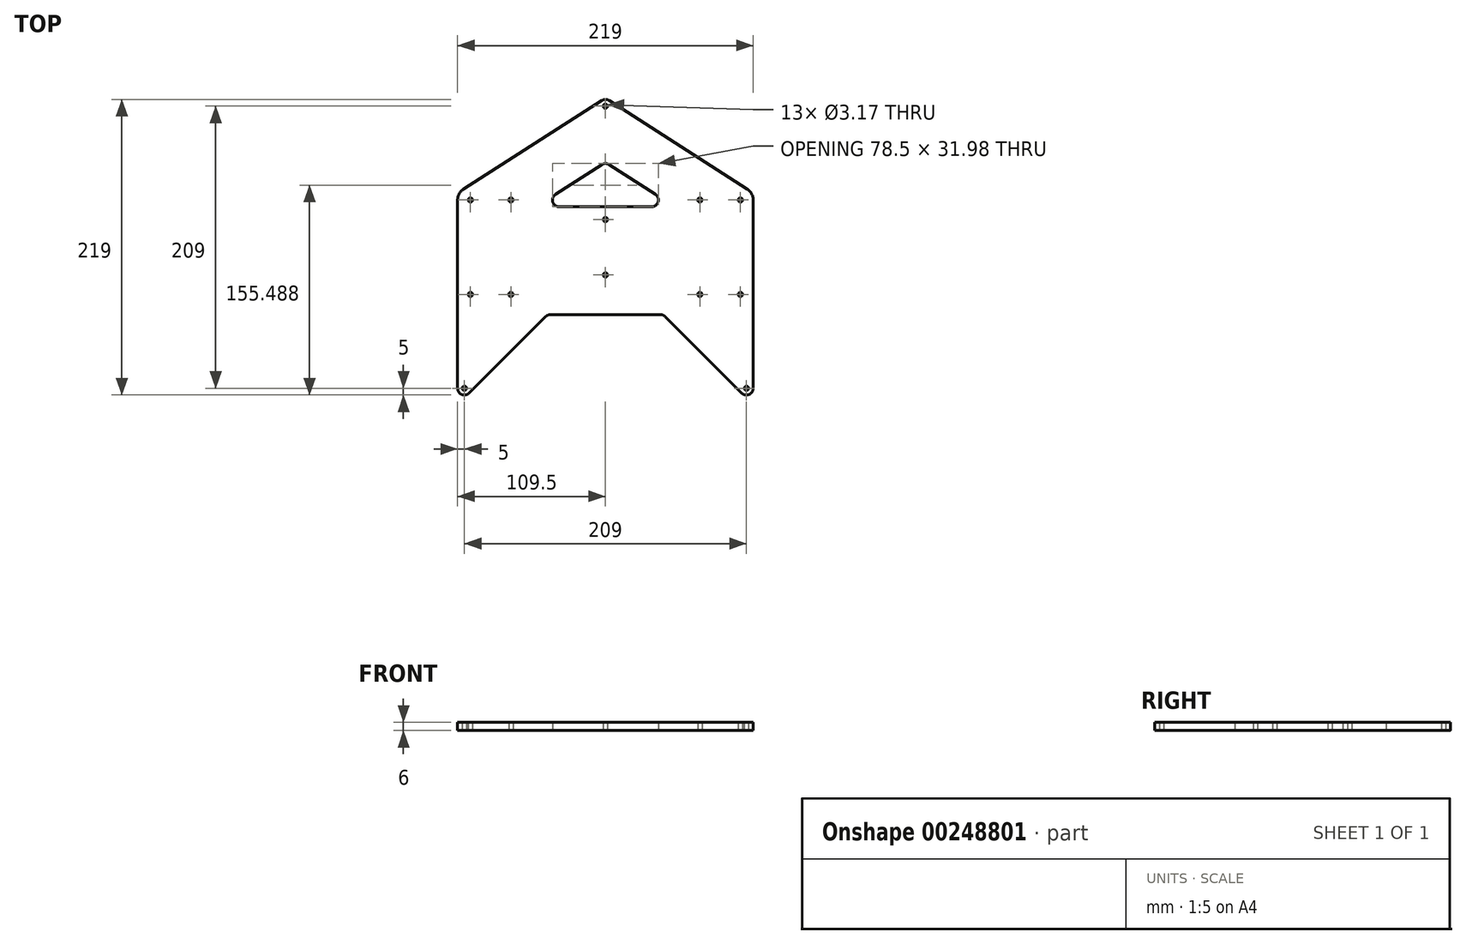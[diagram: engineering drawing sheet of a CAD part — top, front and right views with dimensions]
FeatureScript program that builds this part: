
annotation { "Feature Type Name" : "Feature", "Feature Type Description" : "" }
export const myFeature = defineFeature(function(context is Context, id is Id, definition is map)
    precondition{}
    {
        {
            var Q0;
            Q0=qCreatedBy(makeId("Top.planeOp"),FACE);
            var sketch = newSketch(context, id + "F0", { "sketchPlane" : qUnion([Q0])});
            skCircle(sketch, "E0", {"center": v(0, 20.5) * mm, "radius": 1.59 * mm});
            skCircle(sketch, "E1.MirrorC", {"center": v(0, -20.5) * mm, "radius": 1.59 * mm});
            skLineSegment(sketch, "E2", {"start": v(-100, 35) * mm, "end": v(-70, 35) * mm, "construction": true});
            skPoint(sketch, "E3", {"position": v(-85, 35) * mm});
            skCircle(sketch, "E4", {"center": v(-100, 35) * mm, "radius": 1.59 * mm});
            skCircle(sketch, "E5", {"center": v(-70, 35) * mm, "radius": 1.59 * mm});
            skCircle(sketch, "E6.MirrorC", {"center": v(-70, -35) * mm, "radius": 1.59 * mm});
            skCircle(sketch, "E7.MirrorC", {"center": v(-100, -35) * mm, "radius": 1.59 * mm});
            skLineSegment(sketch, "E8.MirrorCS", {"start": v(-100, -35) * mm, "end": v(-70, -35) * mm, "construction": true});
            skPoint(sketch, "E9.MirrorP", {"position": v(-85, -35) * mm});
            skCircle(sketch, "E10", {"center": v(-104.5, -104.5) * mm, "radius": 1.59 * mm});
            skCircle(sketch, "E11", {"center": v(0, 104.5) * mm, "radius": 1.59 * mm});
            skCircle(sketch, "E12.MirrorC", {"center": v(104.5, -104.5) * mm, "radius": 1.59 * mm});
            skArc(sketch, "E13", {"start": v(-109.5, -104.5) * mm, "mid": v(-106.41, -109.12) * mm, "end": v(-100.96, -108.04) * mm});
            skLineSegment(sketch, "E14", {"start": v(-109.5, -104.5) * mm, "end": v(-109.5, 35) * mm});
            skArc(sketch, "E15", {"start": v(-2.7, 108.7) * mm, "mid": v(-1.4, 109.3) * mm, "end": v(0, 109.5) * mm});
            skArc(sketch, "E16", {"start": v(-109.5, 35) * mm, "mid": v(-108.34, 39.56) * mm, "end": v(-105.13, 43) * mm});
            skLineSegment(sketch, "E17", {"start": v(-105.13, 43) * mm, "end": v(-2.7, 108.7) * mm});
            skPoint(sketch, "E18.orphan", {"position": v(-5, 104.5) * mm});
            skLineSegment(sketch, "E19", {"start": v(-100.96, -108.04) * mm, "end": v(-44.4, -51.46) * mm});
            skLineSegment(sketch, "E20", {"start": v(-40.86, -50) * mm, "end": v(0, -50) * mm});
            skArc(sketch, "E21.MirrorCS", {"start": v(2.7, 108.7) * mm, "mid": v(1.4, 109.3) * mm, "end": v(0, 109.5) * mm});
            skCircle(sketch, "E22.MirrorC", {"center": v(100, 35) * mm, "radius": 1.59 * mm});
            skCircle(sketch, "E23.MirrorC", {"center": v(70, 35) * mm, "radius": 1.59 * mm});
            skCircle(sketch, "E24.MirrorC", {"center": v(70, -35) * mm, "radius": 1.59 * mm});
            skCircle(sketch, "E25.MirrorC", {"center": v(100, -35) * mm, "radius": 1.59 * mm});
            skArc(sketch, "E26.MirrorCS", {"start": v(109.5, 35) * mm, "mid": v(108.34, 39.56) * mm, "end": v(105.13, 43) * mm});
            skArc(sketch, "E27.MirrorCS", {"start": v(109.5, -104.5) * mm, "mid": v(106.41, -109.12) * mm, "end": v(100.96, -108.04) * mm});
            skLineSegment(sketch, "E28.MirrorCS", {"start": v(40.86, -50) * mm, "end": v(0, -50) * mm});
            skLineSegment(sketch, "E29.MirrorCS", {"start": v(100, -35) * mm, "end": v(70, -35) * mm, "construction": true});
            skLineSegment(sketch, "E30.MirrorCS", {"start": v(100, 35) * mm, "end": v(70, 35) * mm, "construction": true});
            skPoint(sketch, "E31.MirrorP", {"position": v(5, 104.5) * mm});
            skLineSegment(sketch, "E32.MirrorCS", {"start": v(109.5, -104.5) * mm, "end": v(109.5, 35) * mm});
            skLineSegment(sketch, "E33.MirrorCS", {"start": v(105.13, 43) * mm, "end": v(2.7, 108.7) * mm});
            skPoint(sketch, "E34.MirrorP", {"position": v(85, 35) * mm});
            skPoint(sketch, "E35.MirrorP", {"position": v(85, -35) * mm});
            skLineSegment(sketch, "E36.MirrorCS", {"start": v(100.96, -108.04) * mm, "end": v(44.4, -51.46) * mm});
            skPoint(sketch, "E37.visualSharp", {"position": v(-42.93, -50) * mm});
            skArc(sketch, "E37.filletArc", {"start": v(-40.86, -50) * mm, "mid": v(-42.77, -50.38) * mm, "end": v(-44.4, -51.46) * mm});
            skPoint(sketch, "E38.visualSharp", {"position": v(42.93, -50) * mm});
            skArc(sketch, "E38.filletArc", {"start": v(44.4, -51.46) * mm, "mid": v(42.77, -50.38) * mm, "end": v(40.86, -50) * mm});
            skLineSegment(sketch, "E39", {"start": v(0, 30) * mm, "end": v(-34.26, 30) * mm});
            skLineSegment(sketch, "E40", {"start": v(-36.96, 39.2) * mm, "end": v(-2.7, 61.18) * mm});
            skLineSegment(sketch, "E41.MirrorCS", {"start": v(36.96, 39.2) * mm, "end": v(2.7, 61.18) * mm});
            skLineSegment(sketch, "E42.MirrorCS", {"start": v(0, 30) * mm, "end": v(34.26, 30) * mm});
            skPoint(sketch, "E43.visualSharp", {"position": v(0, 62.92) * mm});
            skArc(sketch, "E43.filletArc", {"start": v(2.7, 61.18) * mm, "mid": v(0, 61.98) * mm, "end": v(-2.7, 61.18) * mm});
            skPoint(sketch, "E44.visualSharp", {"position": v(-51.3, 30) * mm});
            skArc(sketch, "E44.filletArc", {"start": v(-36.96, 39.2) * mm, "mid": v(-39.05, 33.6) * mm, "end": v(-34.26, 30) * mm});
            skPoint(sketch, "E45.visualSharp", {"position": v(51.3, 30) * mm});
            skArc(sketch, "E45.filletArc", {"start": v(34.26, 30) * mm, "mid": v(39.05, 33.6) * mm, "end": v(36.96, 39.2) * mm});
            skSolve(sketch);
        }
        {
            var Q0;
            Q0=makeQuery(id+"F0.imprint","IMPRINT",FACE,{"disambiguationData":[TD([[makeQuery(id+"F0.imprint","IMPRINT",EDGE,{"derivedFrom":sQuery(id+"F0.wireOp",EDGE,"E0")}),-1.0]])]});
            extrude(context, id + "F1", {"entities" : qUnion([Q0]), "depth" : 6 * mm, "offsetDistance" : 25 * mm});
        }
    });
